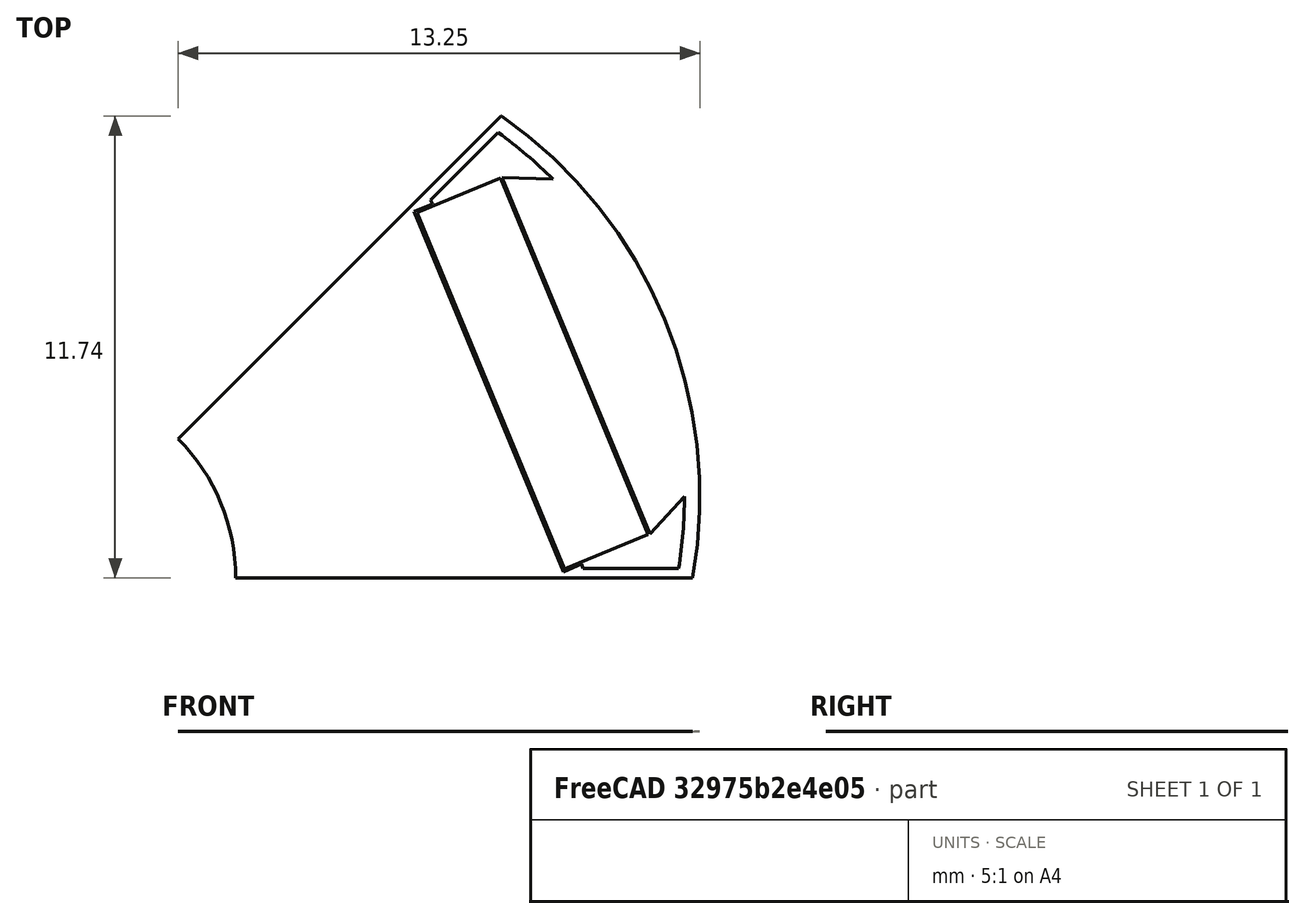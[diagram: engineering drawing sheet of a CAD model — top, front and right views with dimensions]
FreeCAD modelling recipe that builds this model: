
FCSTD DOCUMENT  (FreeCAD 0.18R4 (GitTag))
Label: tRotorClampingPoleShoe
License: All rights reserved
LicenseURL: http://en.wikipedia.org/wiki/All_rights_reserved
objects: Sketcher::SketchObject×6, Surface::Filling×3, PartDesign::Body×2, Spreadsheet::Sheet×1, Part::Cut×1
note: 12 computed .brp shape members not serialized (recipe doc carries the construction recipe); baked Part::Feature solids carry a one-line shape summary decoded from their .brp

FEATURE [Spreadsheet::Sheet] Spreadsheet  label="Variables"
  cells = A2=poleNumber; B2(poleNumber)=8; A3=outerDiameter; B3(outerDiameter)=34.4; D3=Calc Value; A4=innerDiameter; B4(innerDiameter)=10; D4=Input Value; A5=stackLength; B5(stackLength)=15.3; D5=Not Applicable; A6=stackingFactor; B6(stackingFactor)=0.95; A7=embrace; B7(embrace)=68; A8=contourRatio; B8(contourRatio)=68.59999999999999; A9=magnetAirgap; B9(magnetAirgap)=0.05; A10=poleSeparation; B10(poleSeparation)=0.01; A11=magnetWidth; B11(magnetWidth)=9.800000000000001; A12=magnetHeight; B12(magnetHeight)=2.3; A13=rib; B13(rib)=0.5; A14=bridgeCurved; B14(bridgeCurved)=0.39; A15=cutTop; B15(cutTop)=0; A16=cutBottom; B16(cutBottom)=0.5; A17=segmentAngle; B17(segmentAngle)==360 / poleNumber; A18=movePocketInwards; B18(movePocketInwards)=1.27; A19=cuttingThickness; B19(cuttingThickness)=0.1; A20=magnetLength; B20(magnetLength)==stackLength; A21=cut; B21(cut)=0.1; A22=ribShaft; B22(ribShaft)=0; A23=magnetEmbrace; B23(magnetEmbrace)=50; A24=magnetContourRatio; B24(magnetContourRatio)=95; A25=axialMisalignment; B25(axialMisalignment)=0.01; A26=magnetContactRatio; B26(magnetContactRatio)=100; C26=*new
FEATURE [Sketcher::SketchObject] Sketch004  label="BoundingBox"
  MapMode = 5
  Support = -> [XY_Plane]
  expr: Constraints[8] = Variables.outerDiameter
  sketch-geometry (6):
    g0: LineSegment StartX=-17.2 StartY=-17.2 StartZ=0 EndX=17.2 EndY=-17.2 EndZ=0
    g1: LineSegment StartX=17.2 StartY=-17.2 StartZ=0 EndX=17.2 EndY=17.2 EndZ=0
    g2: LineSegment StartX=17.2 StartY=17.2 StartZ=0 EndX=-17.2 EndY=17.2 EndZ=0
    g3: LineSegment StartX=-17.2 StartY=17.2 StartZ=0 EndX=-17.2 EndY=-17.2 EndZ=0
    g4: LineSegment [constr] StartX=-17.2 StartY=-17.2 StartZ=0 EndX=17.2 EndY=17.2 EndZ=0
    g5: GeomPoint X=0 Y=0 Z=0
  constraints (14):
    c: Coincident(g0,g1)
    c: Coincident(g1,g2)
    c: Coincident(g2,g3)
    c: Coincident(g3,g0)
    c: Horizontal(g0)
    c: Horizontal(g2)
    c: Vertical(g1)
    c: Vertical(g3)
    c: DistanceY(g1,g1) = 34.4
    c: Equal(g2,g1)
    c: Coincident(g4,g0)
    c: Coincident(g4,g1)
    c: Symmetric(g0,g1,g5)
    c: Coincident(g-1,g5)
FEATURE [Sketcher::SketchObject] Sketch005  label="RotorSideSketch"
  MapMode = 5
  Support = -> [XY_Plane001]
  expr: Constraints[23] = Variables.stackLength / 2 - Variables.axialMisalignment
  expr: Constraints[19] = Variables.innerDiameter / 2
  expr: Constraints[22] = Variables.stackLength / 2 - Variables.axialMisalignment
  expr: Constraints[9] = Variables.outerDiameter / 2
  expr: Constraints[8] = Variables.innerDiameter / 2
  expr: Constraints[7] = Variables.stackLength
  sketch-geometry (8):
    g0: LineSegment StartX=-7.64 StartY=5 StartZ=0 EndX=7.66 EndY=5 EndZ=0
    g1: LineSegment StartX=7.66 StartY=5 StartZ=0 EndX=7.66 EndY=17.2 EndZ=0
    g2: LineSegment StartX=7.66 StartY=17.2 StartZ=0 EndX=-7.64 EndY=17.2 EndZ=0
    g3: LineSegment StartX=-7.64 StartY=17.2 StartZ=0 EndX=-7.64 EndY=5 EndZ=0
    g4: LineSegment StartX=-7.64 StartY=-5 StartZ=0 EndX=7.66 EndY=-5 EndZ=0
    g5: LineSegment StartX=7.66 StartY=-5 StartZ=0 EndX=7.66 EndY=-17.2 EndZ=0
    g6: LineSegment StartX=7.66 StartY=-17.2 StartZ=0 EndX=-7.64 EndY=-17.2 EndZ=0
    g7: LineSegment StartX=-7.64 StartY=-17.2 StartZ=0 EndX=-7.64 EndY=-5 EndZ=0
  constraints (24):
    c: Coincident(g0,g1)
    c: Coincident(g1,g2)
    c: Coincident(g2,g3)
    c: Coincident(g3,g0)
    c: Horizontal(g0)
    c: Vertical(g1)
    c: Vertical(g3)
    c: DistanceX(g2,g2) = 15.3
    c: DistanceY(g-1,g0) = 5
    c: DistanceY(g-1,g1) = 17.2
    c: Coincident(g4,g5)
    c: Coincident(g5,g6)
    c: Coincident(g6,g7)
    c: Coincident(g7,g4)
    c: Horizontal(g4)
    c: Vertical(g5)
    c: Vertical(g7)
    c: Equal(g4,g0)
    c: Equal(g7,g3)
    c: DistanceY(g4,g-1) = 5
    c: Horizontal(g2)
    c: Horizontal(g6)
    c: DistanceX(g0,g-1) = 7.64
    c: DistanceX(g4,g-1) = 7.64
FEATURE [Sketcher::SketchObject] Sketch006  label="MagnetSideSketch"
  ExternalGeometry = -> [Sketch005]
  MapMode = 5
  Support = -> [XY_Plane001]
  expr: Constraints[23] = Variables.stackLength / 2 - Variables.axialMisalignment
  expr: Constraints[12] = Variables.magnetHeight / 2
  expr: Constraints[8] = Variables.magnetHeight
  expr: Constraints[7] = Variables.magnetLength
  sketch-geometry (9):
    g0: LineSegment StartX=-7.64 StartY=13.75 StartZ=0 EndX=7.66 EndY=13.75 EndZ=0
    g1: LineSegment StartX=7.66 StartY=13.75 StartZ=0 EndX=7.66 EndY=16.05 EndZ=0
    g2: LineSegment StartX=7.66 StartY=16.05 StartZ=0 EndX=-7.64 EndY=16.05 EndZ=0
    g3: LineSegment StartX=-7.64 StartY=16.05 StartZ=0 EndX=-7.64 EndY=13.75 EndZ=0
    g4: LineSegment [constr] StartX=7.66 StartY=16.05 StartZ=0 EndX=7.66 EndY=17.2 EndZ=0
    g5: LineSegment StartX=-7.64 StartY=-16.05 StartZ=0 EndX=7.66 EndY=-16.05 EndZ=0
    g6: LineSegment StartX=7.66 StartY=-16.05 StartZ=0 EndX=7.66 EndY=-13.75 EndZ=0
    g7: LineSegment StartX=7.66 StartY=-13.75 StartZ=0 EndX=-7.64 EndY=-13.75 EndZ=0
    g8: LineSegment StartX=-7.64 StartY=-13.75 StartZ=0 EndX=-7.64 EndY=-16.05 EndZ=0
  constraints (25):
    c: Coincident(g0,g1)
    c: Coincident(g1,g2)
    c: Coincident(g2,g3)
    c: Coincident(g3,g0)
    c: Horizontal(g0)
    c: Vertical(g1)
    c: Vertical(g3)
    c: DistanceX(g2,g2) = 15.3
    c: DistanceY(g1,g1) = 2.3
    c: Coincident(g4,g1)
    c: PointOnObject(g4,g-3)
    c: Angle(g4,g2) = 1.5708
    c: DistanceY(g4,g4) = 1.15
    c: Coincident(g5,g6)
    c: Coincident(g6,g7)
    c: Coincident(g7,g8)
    c: Coincident(g8,g5)
    c: Horizontal(g5)
    c: Vertical(g6)
    c: Vertical(g8)
    c: Symmetric(g7,g0,g-1)
    c: Symmetric(g6,g0,g-1)
    c: Equal(g8,g3)
    c: DistanceX(g0,g-1) = 7.64
    c: Horizontal(g2)
FEATURE [PartDesign::Body] Body001  label="SideView"
  Group = -> [Sketch005,Sketch006]
  Origin = -> Origin001
FEATURE [Sketcher::SketchObject] Sketch008  label="RotorPoleSketch"
  MapMode = 5
  Support = -> [XY_Plane]
  expr: Constraints[34] = Variables.poleSeparation / 2
  expr: Constraints[27] = Variables.innerDiameter / 2
  expr: Constraints[22] = Variables.outerDiameter / 2
  expr: Constraints[26] = Variables.outerDiameter / 2 * Variables.contourRatio / 100
  expr: Constraints[21] = Variables.segmentAngle / 2
  expr: Constraints[10] = Variables.rib / 2
  expr: Constraints[1] = Variables.segmentAngle / 2
  sketch-geometry (16):
    g0: LineSegment [constr] StartX=0 StartY=0 StartZ=0 EndX=17.2 EndY=0 EndZ=0
    g1: LineSegment [constr] StartX=0 StartY=0 StartZ=0 EndX=12.1622 EndY=12.1622 EndZ=0
    g2: LineSegment [constr] StartX=0 StartY=0 StartZ=0 EndX=15.8907 EndY=6.58216 EndZ=0
    g3: ArcOfCircle [constr] CenterX=0 CenterY=0 CenterZ=0 NormalX=0 NormalY=0 NormalZ=1 AngleXU=0 Radius=17.2 StartAngle=0 EndAngle=0.785398
    g4: LineSegment [constr] StartX=0.603553 StartY=0.25 StartZ=0 EndX=12.3377 EndY=11.9842 EndZ=0
    g5: LineSegment [constr] StartX=0.603553 StartY=0.25 StartZ=0 EndX=0.426777 EndY=0.426777 EndZ=0
    g6: LineSegment [constr] StartX=0.603553 StartY=0.25 StartZ=0 EndX=17.1982 EndY=0.25 EndZ=0
    g7: ArcOfCircle CenterX=4.98969 CenterY=2.0668 CenterZ=0 NormalX=0 NormalY=0 NormalZ=1 AngleXU=0 Radius=11.7992 StartAngle=6.10754 EndAngle=7.24423
    g8: ArcOfCircle CenterX=0 CenterY=0 CenterZ=0 NormalX=0 NormalY=0 NormalZ=1 AngleXU=0 Radius=5 StartAngle=0 EndAngle=0.785398
    g9: LineSegment [constr] StartX=0.0120711 StartY=0.005 StartZ=0 EndX=12.1658 EndY=12.1587 EndZ=0
    g10: LineSegment [constr] StartX=0.0120711 StartY=0.005 StartZ=0 EndX=0.00853553 EndY=0.00853553 EndZ=0
    g11: LineSegment [constr] StartX=0.0120711 StartY=0.005 StartZ=0 EndX=17.2 EndY=0.005 EndZ=0
    g12: LineSegment StartX=11.7467 StartY=11.7396 StartZ=0 EndX=11.7432 EndY=11.7432 EndZ=0
    g13: LineSegment StartX=16.6074 StartY=0.005 StartZ=0 EndX=16.6074 EndY=0 EndZ=0
    g14: LineSegment StartX=3.53553 StartY=3.53553 StartZ=0 EndX=11.7432 EndY=11.7432 EndZ=0
    g15: LineSegment StartX=5 StartY=0 StartZ=0 EndX=16.6074 EndY=0 EndZ=0
  constraints (50):
    c: Coincident(g2,g-1)
    c: Angle(g0,g2) = 0.392699
    c: Coincident(g3,g0)
    c: PointOnObject(g2,g3)
    c: PointOnObject(g4,g2)
    c: PointOnObject(g4,g3)
    c: Parallel(g1,g4)
    c: Coincident(g5,g4)
    c: PointOnObject(g5,g1)
    c: Angle(g5,g1) = 1.5708
    c: Distance(g5) = 0.25
    c: Coincident(g6,g4)
    c: PointOnObject(g6,g3)
    c: Parallel(g6,g0)
    c: Coincident(g3,g1)
    c: Coincident(g0,g-1)
    c: Coincident(g1,g-1)
    c: Angle(g-1,g0) = 0
    c: PointOnObject(g7,g2)
    c: PointOnObject(g2,g7)
    c: Coincident(g3,g-1)
    c: Angle(g2,g1) = 0.392699
    c: Distance(g2) = 17.2
    c: Coincident(g8,g-1)
    c: PointOnObject(g8,g1)
    c: PointOnObject(g8,g0)
    c: Radius(g7) = 11.7992
    c: Radius(g8) = 5
    c: PointOnObject(g9,g2)
    c: PointOnObject(g9,g3)
    c: Parallel(g9,g1)
    c: Coincident(g10,g9)
    c: PointOnObject(g10,g1)
    c: Angle(g10,g1) = 1.5708
    c: Distance(g10) = 0.005
    c: Coincident(g11,g9)
    c: PointOnObject(g11,g3)
    c: Parallel(g11,g0)
    c: PointOnObject(g7,g9)
    c: PointOnObject(g7,g11)
    c: Coincident(g12,g7)
    c: PointOnObject(g12,g1)
    c: Angle(g1,g12) = 1.5708
    c: Coincident(g13,g7)
    c: PointOnObject(g13,g0)
    c: Angle(g13,g0) = 1.5708
    c: Coincident(g14,g8)
    c: Coincident(g14,g12)
    c: Coincident(g15,g8)
    c: Coincident(g15,g13)
FEATURE [Surface::Filling] Surface  label="RotorPoleSketch_Surface"
  Anisotropy = false
  BoundaryEdges = -> [Sketch008]
  BoundaryOrder = [0,0,0,0,0,0]
  Degree = 3
  Iterations = 2
  MaximumDegree = 8
  MaximumSegments = 9
  PointsOnCurve = 15
  TolAngular = 0.01
  TolCurvature = 0.1
  Tolerance2d = 1e-05
  Tolerance3d = 0.0001
FEATURE [Sketcher::SketchObject] Sketch009  label="PocketSketch"
  MapMode = 5
  Support = -> [XY_Plane]
  expr: Constraints[121] = Variables.movePocketInwards
  expr: Constraints[117] = Variables.magnetHeight + 2 * Variables.magnetAirgap
  expr: Constraints[99] = Variables.magnetWidth / 2 + Variables.magnetAirgap
  expr: Constraints[34] = Variables.poleSeparation / 2
  expr: Constraints[79] = Variables.magnetWidth / 2 * Variables.magnetContactRatio / 100
  expr: Constraints[54] = Variables.segmentAngle / 2 * Variables.embrace / 100
  expr: Constraints[62] = Variables.bridgeCurved
  expr: Constraints[105] = Variables.magnetWidth / 2 + Variables.magnetAirgap
  expr: Constraints[78] = Variables.magnetWidth / 2 * Variables.magnetContactRatio / 100
  expr: Constraints[26] = Variables.outerDiameter / 2 * Variables.contourRatio / 100
  expr: Constraints[91] = Variables.cutBottom
  expr: Constraints[10] = Variables.rib / 2
  expr: Constraints[55] = Variables.segmentAngle / 2 * Variables.embrace / 100
  expr: Constraints[22] = Variables.outerDiameter / 2
  expr: Constraints[27] = Variables.innerDiameter / 2
  expr: Constraints[21] = Variables.segmentAngle / 2
  expr: Constraints[1] = Variables.segmentAngle / 2
  sketch-geometry (42):
    g0: LineSegment [constr] StartX=0 StartY=0 StartZ=0 EndX=17.2 EndY=0 EndZ=0
    g1: LineSegment [constr] StartX=0 StartY=0 StartZ=0 EndX=12.1622 EndY=12.1622 EndZ=0
    g2: LineSegment [constr] StartX=0 StartY=0 StartZ=0 EndX=15.8907 EndY=6.58216 EndZ=0
    g3: ArcOfCircle [constr] CenterX=0 CenterY=0 CenterZ=0 NormalX=0 NormalY=0 NormalZ=1 AngleXU=0 Radius=17.2 StartAngle=0 EndAngle=0.785398
    g4: LineSegment [constr] StartX=0.603553 StartY=0.25 StartZ=0 EndX=12.3377 EndY=11.9842 EndZ=0
    g5: LineSegment [constr] StartX=0.603553 StartY=0.25 StartZ=0 EndX=0.426777 EndY=0.426777 EndZ=0
    g6: LineSegment [constr] StartX=0.603553 StartY=0.25 StartZ=0 EndX=17.1982 EndY=0.25 EndZ=0
    g7: ArcOfCircle [constr] CenterX=4.98969 CenterY=2.0668 CenterZ=0 NormalX=0 NormalY=0 NormalZ=1 AngleXU=0 Radius=11.7992 StartAngle=6.10754 EndAngle=7.24423
    g8: ArcOfCircle [constr] CenterX=0 CenterY=0 CenterZ=0 NormalX=0 NormalY=0 NormalZ=1 AngleXU=0 Radius=5 StartAngle=0 EndAngle=0.785398
    g9: LineSegment [constr] StartX=0.0120711 StartY=0.005 StartZ=0 EndX=12.1658 EndY=12.1587 EndZ=0
    g10: LineSegment [constr] StartX=0.0120711 StartY=0.005 StartZ=0 EndX=0.00853553 EndY=0.00853553 EndZ=0
    g11: LineSegment [constr] StartX=0.0120711 StartY=0.005 StartZ=0 EndX=17.2 EndY=0.005 EndZ=0
    g12: LineSegment [constr] StartX=11.7467 StartY=11.7396 StartZ=0 EndX=11.7432 EndY=11.7432 EndZ=0
    g13: LineSegment [constr] StartX=16.6074 StartY=0.005 StartZ=0 EndX=16.6074 EndY=0 EndZ=0
    g14: LineSegment [constr] StartX=3.53553 StartY=3.53553 StartZ=0 EndX=11.7432 EndY=11.7432 EndZ=0
    g15: LineSegment [constr] StartX=5 StartY=0 StartZ=0 EndX=16.6074 EndY=0 EndZ=0
    g16: LineSegment [constr] StartX=0 StartY=0 StartZ=0 EndX=13.3712 EndY=10.3717 EndZ=0
    g17: LineSegment [constr] StartX=0 StartY=0 StartZ=0 EndX=16.7888 EndY=2.12091 EndZ=0
    g18: ArcOfCircle [constr] CenterX=4.98969 CenterY=2.0668 CenterZ=0 NormalX=0 NormalY=0 NormalZ=1 AngleXU=0 Radius=11.4092 StartAngle=0.000426374 EndAngle=0.945319
    g19: LineSegment [constr] StartX=15.8907 StartY=6.58216 StartZ=0 EndX=15.5304 EndY=6.43291 EndZ=0
    g20: ArcOfCircle CenterX=4.98969 CenterY=2.0668 CenterZ=0 NormalX=0 NormalY=0 NormalZ=1 AngleXU=0 Radius=11.4092 StartAngle=0.784972 EndAngle=0.945319
    g21: ArcOfCircle CenterX=4.98969 CenterY=2.0668 CenterZ=0 NormalX=0 NormalY=0 NormalZ=1 AngleXU=0 Radius=11.4092 StartAngle=6.12326 EndAngle=6.28361
    g22: LineSegment [constr] StartX=13.0607 StartY=10.1309 StartZ=0 EndX=16.3989 EndY=2.07166 EndZ=0
    g23: LineSegment [constr] StartX=14.7298 StartY=6.10127 StartZ=0 EndX=13.6458 EndY=5.65226 EndZ=0
    g24: LineSegment [constr] StartX=13.6458 StartY=5.65226 StartZ=0 EndX=11.7706 EndY=10.1793 EndZ=0
    g25: LineSegment [constr] StartX=13.6458 StartY=5.65226 StartZ=0 EndX=15.5209 EndY=1.12525 EndZ=0
    g26: LineSegment StartX=11.7706 StartY=10.1793 StartZ=0 EndX=13.0607 EndY=10.1309 EndZ=0
    g27: LineSegment StartX=15.5209 StartY=1.12525 StartZ=0 EndX=16.3989 EndY=2.07166 EndZ=0
    g28: LineSegment [constr] StartX=9.95387 StartY=9.60032 StartZ=0 EndX=13.8269 EndY=0.25 EndZ=0
    g29: LineSegment StartX=9.95387 StartY=9.60032 StartZ=0 EndX=11.6696 EndY=11.316 EndZ=0
    g30: LineSegment StartX=13.8269 StartY=0.25 StartZ=0 EndX=16.2533 EndY=0.25 EndZ=0
    g31: LineSegment [constr] StartX=11.8904 StartY=4.92516 StartZ=0 EndX=11.4284 EndY=4.73382 EndZ=0
    g32: LineSegment [constr] StartX=11.4284 StartY=4.73382 StartZ=0 EndX=9.53416 EndY=9.30702 EndZ=0
    g33: LineSegment [constr] StartX=11.4284 StartY=4.73382 StartZ=0 EndX=13.3227 EndY=0.160613 EndZ=0
    g34: LineSegment StartX=9.53416 StartY=9.30702 StartZ=0 EndX=9.9961 EndY=9.49836 EndZ=0
    g35: LineSegment StartX=9.9961 StartY=9.49836 StartZ=0 EndX=9.95387 EndY=9.60032 EndZ=0
    g36: LineSegment StartX=13.3227 StartY=0.160613 StartZ=0 EndX=13.7847 EndY=0.351955 EndZ=0
    g37: LineSegment StartX=13.7847 StartY=0.351955 StartZ=0 EndX=13.8269 EndY=0.25 EndZ=0
    g38: LineSegment StartX=9.53416 StartY=9.30702 StartZ=0 EndX=13.3227 EndY=0.160613 EndZ=0
    g39: LineSegment StartX=11.7706 StartY=10.1793 StartZ=0 EndX=15.5209 EndY=1.12525 EndZ=0
    g40: LineSegment [constr] StartX=11.4284 StartY=4.73382 StartZ=0 EndX=13.6458 EndY=5.65226 EndZ=0
    g41: LineSegment [constr] StartX=16.3989 StartY=2.07166 StartZ=0 EndX=15.1289 EndY=2.07166 EndZ=0
  constraints (122):
    c: Coincident(g2,g-1)
    c: Angle(g0,g2) = 0.392699
    c: Coincident(g3,g0)
    c: PointOnObject(g2,g3)
    c: PointOnObject(g4,g2)
    c: PointOnObject(g4,g3)
    c: Parallel(g1,g4)
    c: Coincident(g5,g4)
    c: PointOnObject(g5,g1)
    c: Angle(g5,g1) = 1.5708
    c: Distance(g5) = 0.25
    c: Coincident(g6,g4)
    c: PointOnObject(g6,g3)
    c: Parallel(g6,g0)
    c: Coincident(g3,g1)
    c: Coincident(g0,g-1)
    c: Coincident(g1,g-1)
    c: Angle(g-1,g0) = 0
    c: PointOnObject(g7,g2)
    c: PointOnObject(g2,g7)
    c: Coincident(g3,g-1)
    c: Angle(g2,g1) = 0.392699
    c: Distance(g2) = 17.2
    c: Coincident(g8,g-1)
    c: PointOnObject(g8,g1)
    c: PointOnObject(g8,g0)
    c: Radius(g7) = 11.7992
    c: Radius(g8) = 5
    c: PointOnObject(g9,g2)
    c: PointOnObject(g9,g3)
    c: Parallel(g9,g1)
    c: Coincident(g10,g9)
    c: PointOnObject(g10,g1)
    c: Angle(g10,g1) = 1.5708
    c: Distance(g10) = 0.005
    c: Coincident(g11,g9)
    c: PointOnObject(g11,g3)
    c: Parallel(g11,g0)
    c: PointOnObject(g7,g9)
    c: PointOnObject(g7,g11)
    c: Coincident(g12,g7)
    c: PointOnObject(g12,g1)
    c: Angle(g1,g12) = 1.5708
    c: Coincident(g13,g7)
    c: PointOnObject(g13,g0)
    c: Angle(g13,g0) = 1.5708
    c: Coincident(g14,g8)
    c: Coincident(g14,g12)
    c: Coincident(g15,g8)
    c: Coincident(g15,g13)
    c: Coincident(g16,g-1)
    c: PointOnObject(g16,g7)
    c: Coincident(g17,g16)
    c: PointOnObject(g17,g7)
    c: Angle(g2,g16) = 0.267035
    c: Angle(g17,g2) = 0.267035
    c: Coincident(g18,g7)
    c: PointOnObject(g18,g4)
    c: PointOnObject(g18,g17)
    c: Coincident(g19,g2)
    c: PointOnObject(g19,g18)
    c: Parallel(g19,g2)
    c: Distance(g19) = 0.39
    c: Coincident(g20,g7)
    c: Coincident(g20,g18)
    c: PointOnObject(g20,g16)
    c: Coincident(g21,g20)
    c: Coincident(g21,g18)
    c: PointOnObject(g21,g6)
    c: Coincident(g22,g20)
    c: Coincident(g22,g21)
    c: PointOnObject(g23,g22)
    c: PointOnObject(g23,g2)
    c: PointOnObject(g23,g2)
    c: Coincident(g24,g23)
    c: Coincident(g25,g24)
    c: Angle(g24,g2) = 1.5708
    c: Angle(g2,g25) = 1.5708
    c: Distance(g24) = 4.9
    c: Distance(g25) = 4.9
    c: Coincident(g26,g24)
    c: Coincident(g26,g20)
    c: Coincident(g27,g25)
    c: Coincident(g27,g21)
    c: PointOnObject(g28,g4)
    c: PointOnObject(g28,g6)
    c: Angle(g2,g28) = 1.5708
    c: Coincident(g29,g28)
    c: Coincident(g29,g20)
    c: Coincident(g30,g28)
    c: Coincident(g30,g21)
    c: Distance(g31) = 0.5
    c: PointOnObject(g31,g2)
    c: PointOnObject(g31,g28)
    c: PointOnObject(g31,g2)
    c: Coincident(g32,g31)
    c: Coincident(g33,g32)
    c: Angle(g32,g2) = 1.5708
    c: Angle(g2,g33) = 1.5708
    c: Distance(g32) = 4.95
    c: Coincident(g34,g32)
    c: PointOnObject(g34,g28)
    c: Angle(g32,g34) = 1.5708
    c: Coincident(g35,g34)
    c: Coincident(g35,g29)
    c: Distance(g33) = 4.95
    c: Coincident(g36,g33)
    c: Angle(g36,g33) = 1.5708
    c: PointOnObject(g36,g28)
    c: Coincident(g37,g36)
    c: Coincident(g37,g30)
    c: Coincident(g38,g34)
    c: Coincident(g38,g36)
    c: Coincident(g39,g26)
    c: Coincident(g39,g27)
    c: Coincident(g40,g31)
    c: Coincident(g40,g23)
    c: Distance(g40) = 2.4
    c: Coincident(g41,g21)
    c: PointOnObject(g41,g39)
    c: Parallel(g41,g30)
    c: Distance(g41) = 1.27
FEATURE [Surface::Filling] Surface001  label="PocketSketch_Surface"
  Anisotropy = false
  BoundaryEdges = -> [Sketch009]
  BoundaryOrder = [0,0,0,0,0,0,0,0,0,0,0,0,0,0,0,0]
  Degree = 3
  Iterations = 2
  MaximumDegree = 8
  MaximumSegments = 9
  PointsOnCurve = 15
  TolAngular = 0.01
  TolCurvature = 0.1
  Tolerance2d = 1e-05
  Tolerance3d = 0.0001
FEATURE [Part::Cut] Cut  label="Rotor_Surface"
  Base = -> Surface
  Tool = -> Surface001
FEATURE [Sketcher::SketchObject] Sketch010  label="MagnetSketch"
  ExternalGeometry = -> [Sketch009]
  MapMode = 2
  Support = -> [Sketch009]
  expr: Constraints[21] = Variables.magnetAirgap
  expr: Constraints[11] = Variables.magnetHeight
  expr: Constraints[5] = Variables.magnetWidth / 2
  expr: Constraints[4] = Variables.magnetWidth / 2
  sketch-geometry (8):
    g0: LineSegment [constr] StartX=0 StartY=0 StartZ=0 EndX=11.4284 EndY=4.73382 EndZ=0
    g1: LineSegment [constr] StartX=11.4746 StartY=4.75295 StartZ=0 EndX=9.59949 EndY=9.27996 EndZ=0
    g2: LineSegment [constr] StartX=11.4746 StartY=4.75295 StartZ=0 EndX=13.3498 EndY=0.225941 EndZ=0
    g3: LineSegment StartX=9.59949 StartY=9.27996 StartZ=0 EndX=11.7244 EndY=10.1601 EndZ=0
    g4: LineSegment StartX=9.59949 StartY=9.27996 StartZ=0 EndX=13.3498 EndY=0.225941 EndZ=0
    g5: LineSegment StartX=13.3498 StartY=0.225941 StartZ=0 EndX=15.4747 EndY=1.10611 EndZ=0
    g6: LineSegment StartX=11.7244 StartY=10.1601 StartZ=0 EndX=15.4747 EndY=1.10611 EndZ=0
    g7: LineSegment [constr] StartX=11.4284 StartY=4.73382 StartZ=0 EndX=11.4746 EndY=4.75295 EndZ=0
  constraints (22):
    c: Angle(g0,g-4) = 1.5708
    c: Coincident(g0,g-1)
    c: Angle(g1,g0) = 1.5708
    c: Angle(g0,g2) = 1.5708
    c: Distance(g2) = 4.9
    c: Distance(g1) = 4.9
    c: Angle(g1,g3) = 1.5708
    c: Coincident(g3,g1)
    c: PointOnObject(g2,g0)
    c: Coincident(g4,g3)
    c: Coincident(g4,g2)
    c: Distance(g3) = 2.3
    c: Angle(g5,g4) = 1.5708
    c: Coincident(g6,g5)
    c: Coincident(g5,g4)
    c: Angle(g6,g5) = 1.5708
    c: Coincident(g3,g6)
    c: PointOnObject(g0,g-4)
    c: Coincident(g1,g2)
    c: Coincident(g7,g0)
    c: Coincident(g7,g1)
    c: Distance(g7) = 0.05
FEATURE [PartDesign::Body] Body  label="TopView"
  Group = -> [Sketch004,Sketch008,Sketch009,Sketch010]
  Origin = -> Origin
FEATURE [Surface::Filling] Surface002  label="Magnet_Surface"
  Anisotropy = false
  BoundaryEdges = -> [Sketch010]
  BoundaryOrder = [0,0,0,0]
  Degree = 3
  Iterations = 2
  MaximumDegree = 8
  MaximumSegments = 9
  PointsOnCurve = 15
  TolAngular = 0.01
  TolCurvature = 0.1
  Tolerance2d = 1e-05
  Tolerance3d = 0.0001
